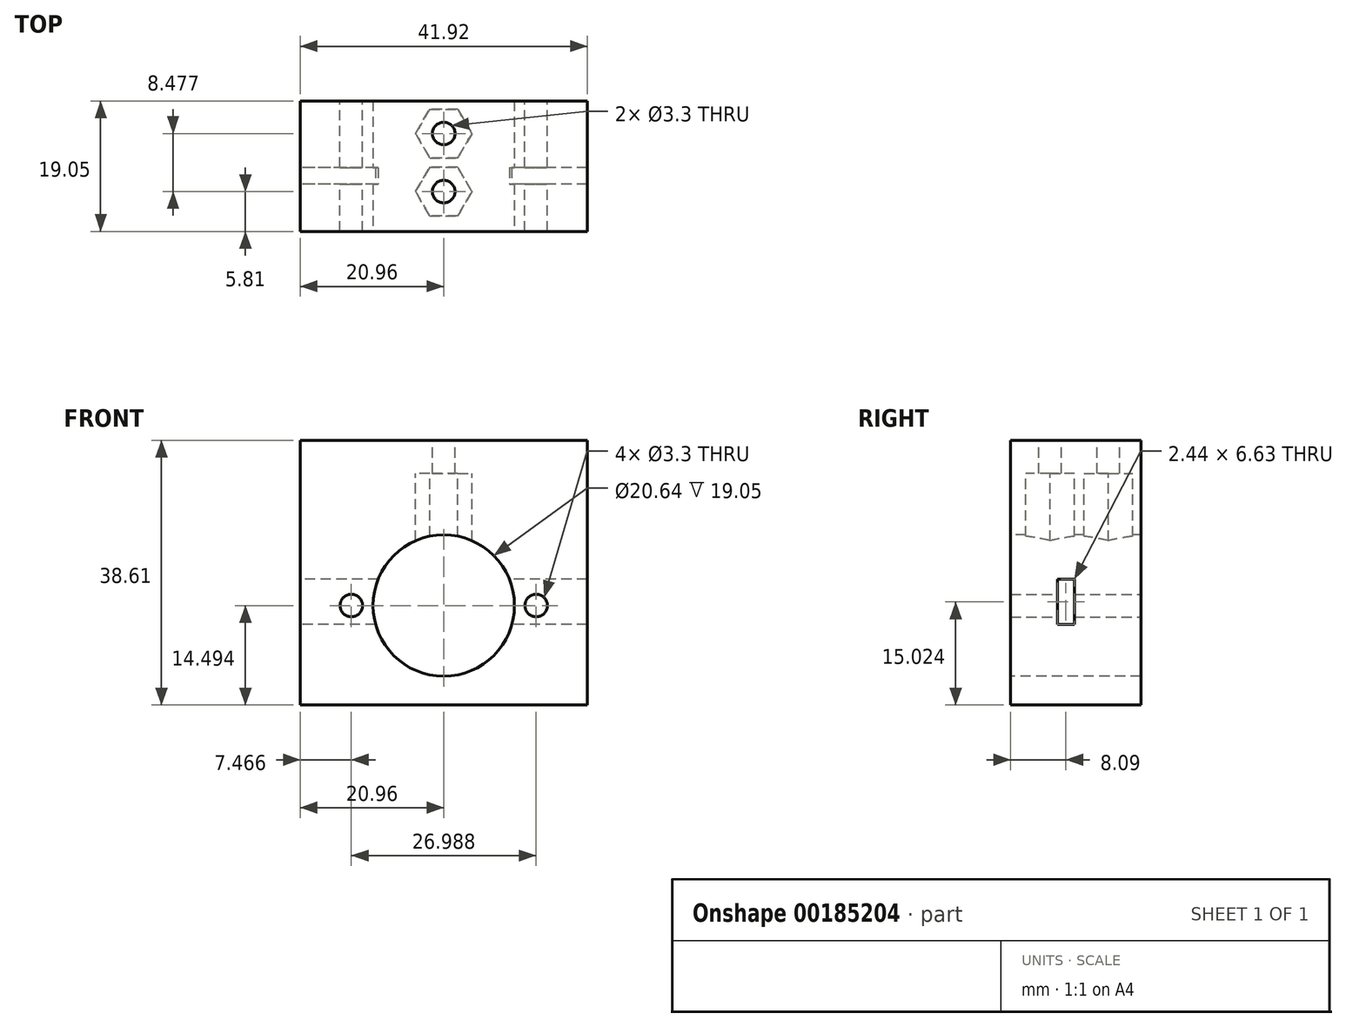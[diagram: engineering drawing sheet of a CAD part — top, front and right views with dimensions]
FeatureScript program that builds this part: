
annotation { "Feature Type Name" : "Feature", "Feature Type Description" : "" }
export const myFeature = defineFeature(function(context is Context, id is Id, definition is map)
    precondition{}
    {
        {
            var Q0;
            Q0=qCreatedBy(makeId("Front.planeOp"),FACE);
            var sketch = newSketch(context, id + "F0", { "sketchPlane" : qUnion([Q0])});
            skLineSegment(sketch, "E0.bottom", {"start": v(20.96, -17.65) * mm, "end": v(-20.96, -17.65) * mm});
            skLineSegment(sketch, "E0.top", {"start": v(20.96, 17.65) * mm, "end": v(-20.96, 17.65) * mm});
            skLineSegment(sketch, "E0.left", {"start": v(20.96, -17.65) * mm, "end": v(20.96, 17.65) * mm});
            skLineSegment(sketch, "E0.right", {"start": v(-20.96, -17.65) * mm, "end": v(-20.96, 17.65) * mm});
            skPoint(sketch, "E0.middle", {"position": v(0, 0) * mm});
            skSolve(sketch);
        }
        {
            var Q0;
            Q0=makeQuery(id+"F0.imprint","IMPRINT",FACE,{"disambiguationData":[TD([[makeQuery(id+"F0.imprint","IMPRINT",EDGE,{"derivedFrom":sQuery(id+"F0.wireOp",EDGE,"E0.bottom")}),-1.0]])]});
            extrude(context, id + "F1", {"entities" : qUnion([Q0]), "depth" : 19.05 * mm});
        }
        {
            var Q0;
            Q0=makeQuery(id+"F1.opExtrude","CAP_FACE",FACE,{"disambiguationData":[OSD([sQuery(id+"F0.wireOp",EDGE,"E0.bottom"),sQuery(id+"F0.wireOp",EDGE,"E0.top"),sQuery(id+"F0.wireOp",EDGE,"E0.left"),sQuery(id+"F0.wireOp",EDGE,"E0.right")])],"isStart":false});
            var sketch = newSketch(context, id + "F2", { "sketchPlane" : qUnion([Q0])});
            skCircle(sketch, "E1", {"center": v(0, -6.47) * mm, "radius": 10.32 * mm});
            skSolve(sketch);
        }
        {
            var Q0;
            Q0=makeQuery(id+"F2.imprint","IMPRINT",FACE,{"disambiguationData":[TD([[makeQuery(id+"F2.imprint","IMPRINT",EDGE,{"derivedFrom":sQuery(id+"F2.wireOp",EDGE,"E1")}),1.0]])]});
            var Q1;
            Q1=sQuery(id+"F2.wireOp",EDGE,"E1");
            var Q2;
            Q2=makeQuery(id+"F1.opExtrude","SWEPT_BODY",BODY,{"disambiguationData":[OSD([sQuery(id+"F0.wireOp",EDGE,"E0.bottom"),sQuery(id+"F0.wireOp",EDGE,"E0.top"),sQuery(id+"F0.wireOp",EDGE,"E0.left"),sQuery(id+"F0.wireOp",EDGE,"E0.right")])]});
            extrude(context, id + "F3", {"entities" : qUnion([Q0]), "operationType" : NewBodyOperationType.REMOVE, "surfaceEntities" : qUnion([Q1]), "endBound" : BoundingType.UP_TO_BODY, "oppositeDirection" : true, "endBoundEntityBody" : qUnion([Q2]), "depth" : 25.4 * mm});
        }
        {
            var Q0;
            Q0=makeQuery(id+"F1.opExtrude","SWEPT_FACE",FACE,{"disambiguationData":[OSD([sQuery(id+"F0.wireOp",EDGE,"E0.top")])]});
            var sketch = newSketch(context, id + "F4", { "sketchPlane" : qUnion([Q0])});
            skLineSegment(sketch, "E2", {"start": v(0, -4.76) * mm, "end": v(0, -14.29) * mm});
            skCircle(sketch, "E3.cCircle", {"center": v(0, -4.76) * mm, "radius": 3.56 * mm, "construction": true});
            skLineSegment(sketch, "E3.0", {"start": v(2.05, -8.32) * mm, "end": v(-2.05, -8.32) * mm});
            skLineSegment(sketch, "E3.1", {"start": v(-2.05, -8.32) * mm, "end": v(-4.1, -4.76) * mm});
            skLineSegment(sketch, "E3.2", {"start": v(-4.1, -4.76) * mm, "end": v(-2.05, -1.2) * mm});
            skLineSegment(sketch, "E3.3", {"start": v(-2.05, -1.2) * mm, "end": v(2.05, -1.2) * mm});
            skLineSegment(sketch, "E3.4", {"start": v(2.05, -1.2) * mm, "end": v(4.1, -4.76) * mm});
            skLineSegment(sketch, "E3.5", {"start": v(4.1, -4.76) * mm, "end": v(2.05, -8.32) * mm});
            skPoint(sketch, "E3.0.midPoint", {"position": v(0, -8.32) * mm});
            skCircle(sketch, "E4.cCircle", {"center": v(0, -13.24) * mm, "radius": 3.56 * mm, "construction": true});
            skPoint(sketch, "E4.0.midPoint", {"position": v(0.3, -16.78) * mm});
            skLineSegment(sketch, "E5.0", {"start": v(2.05, -16.8) * mm, "end": v(-2.05, -16.8) * mm});
            skLineSegment(sketch, "E5.1", {"start": v(-2.05, -16.8) * mm, "end": v(-4.1, -13.24) * mm});
            skLineSegment(sketch, "E5.2", {"start": v(-4.1, -13.24) * mm, "end": v(-2.05, -9.68) * mm});
            skLineSegment(sketch, "E5.3", {"start": v(-2.05, -9.68) * mm, "end": v(2.05, -9.68) * mm});
            skLineSegment(sketch, "E5.4", {"start": v(2.05, -9.68) * mm, "end": v(4.1, -13.24) * mm});
            skLineSegment(sketch, "E5.5", {"start": v(4.1, -13.24) * mm, "end": v(2.05, -16.8) * mm});
            skPoint(sketch, "E5.0.midPoint", {"position": v(0, -16.8) * mm});
            skSolve(sketch);
        }
        {
            var Q0;
            Q0=makeQuery(id+"F4.imprint","IMPRINT",FACE,{"disambiguationData":[TD([[makeQuery(id+"F4.imprint","IMPRINT",EDGE,{"derivedFrom":sQuery(id+"F4.wireOp",EDGE,"E5.0")}),-1.0]])]});
            var Q1;
            {var subQ1=sQuery(id+"F4.wireOp",EDGE,"E3.1");Q1=makeQuery(id+"F4.imprint","IMPRINT",FACE,{"disambiguationData":[TD([[makeQuery(id+"F4.imprint","IMPRINT",EDGE,{"derivedFrom":subQ1}),-1.0]])]});}
            extrude(context, id + "F5", {"entities" : qUnion([Q0, Q1]), "operationType" : NewBodyOperationType.REMOVE, "endBound" : BoundingType.UP_TO_NEXT, "oppositeDirection" : true, "depth" : 25.4 * mm});
        }
        {
            var Q0;
            Q0=makeQuery(id+"F1.opExtrude","SWEPT_FACE",FACE,{"disambiguationData":[OSD([sQuery(id+"F0.wireOp",EDGE,"E0.top")])]});
            extrude(context, id + "F6", {"entities" : qUnion([Q0]), "operationType" : NewBodyOperationType.ADD, "oppositeDirection" : true, "depth" : 5.84 * mm});
        }
        {
            var Q0;
            Q0=makeQuery(id+"F1.opExtrude","SWEPT_FACE",FACE,{"disambiguationData":[OSD([sQuery(id+"F0.wireOp",EDGE,"E0.left")])]});
            var sketch = newSketch(context, id + "F7", { "sketchPlane" : qUnion([Q0])});
            skLineSegment(sketch, "E6.0", {"start": v(-19.05, 12.83) * mm, "end": v(0, 12.83) * mm});
            skSolve(sketch);
        }
        {
            var Q0;
            {var subQ0=sQuery(id+"F7.wireOp",EDGE,"E6.0");Q0=makeQuery(id+"F7.imprint","IMPRINT",FACE,{"disambiguationData":[TD([[makeQuery(id+"F7.imprint","IMPRINT",EDGE,{"derivedFrom":subQ0}),1.0]])]});}
            extrude(context, id + "F8", {"entities" : qUnion([Q0]), "operationType" : NewBodyOperationType.ADD, "oppositeDirection" : true, "depth" : 25.4 * mm});
        }
        {
            var Q0;
            Q0=sQuery(id+"F4.wireOp",VERTEX,"E3.cCircle.center");
            var Q1;
            Q1=sQuery(id+"F4.wireOp",VERTEX,"E4.cCircle.center");
            var Q2;
            Q2=makeQuery(id+"F1.opExtrude","SWEPT_BODY",BODY,{"disambiguationData":[OSD([sQuery(id+"F0.wireOp",EDGE,"E0.bottom"),sQuery(id+"F0.wireOp",EDGE,"E0.top"),sQuery(id+"F0.wireOp",EDGE,"E0.left"),sQuery(id+"F0.wireOp",EDGE,"E0.right")])]});
            hole(context, id + "F9", {"style" : HoleStyle.SIMPLE, "endStyle" : HoleEndStyle.BLIND, "standardTappedOrClearance" : lookupTablePath({ "standard" : "ISO", "fit" : "Normal", "size" : "M3", "type" : "Clearance" }), "standardBlindInLast" : lookupTablePath({ "fit" : "Standard", "standard" : "ISO", "size" : "M3", "type" : "Clearance" }), "holeDiameter" : 3.3 * mm, "holeDepth" : 12.7 * mm, "startFromSketch" : true, "locations" : qUnion([Q0, Q1]), "scope" : qUnion([Q2])});
        }
        {
            var Q0;
            Q0=makeQuery(id+"F1.opExtrude","CAP_FACE",FACE,{"disambiguationData":[OSD([sQuery(id+"F0.wireOp",EDGE,"E0.bottom"),sQuery(id+"F0.wireOp",EDGE,"E0.top"),sQuery(id+"F0.wireOp",EDGE,"E0.left"),sQuery(id+"F0.wireOp",EDGE,"E0.right")])],"isStart":true});
            var sketch = newSketch(context, id + "F10", { "sketchPlane" : qUnion([Q0])});
            skLineSegment(sketch, "E7", {"start": v(-13.5, -6.47) * mm, "end": v(13.5, -6.47) * mm});
            skSolve(sketch);
        }
        {
            var Q0;
            Q0=sQuery(id+"F10.wireOp",VERTEX,"E7.start");
            var Q1;
            Q1=sQuery(id+"F10.wireOp",VERTEX,"E7.end");
            var Q2;
            Q2=makeQuery(id+"F1.opExtrude","SWEPT_BODY",BODY,{"disambiguationData":[OSD([sQuery(id+"F0.wireOp",EDGE,"E0.bottom"),sQuery(id+"F0.wireOp",EDGE,"E0.top"),sQuery(id+"F0.wireOp",EDGE,"E0.left"),sQuery(id+"F0.wireOp",EDGE,"E0.right")])]});
            hole(context, id + "F11", {"style" : HoleStyle.SIMPLE, "endStyle" : HoleEndStyle.THROUGH, "holeDiameter" : 3.3 * mm, "startFromSketch" : true, "locations" : qUnion([Q0, Q1]), "scope" : qUnion([Q2]), "isTappedThrough" : true});
        }
        {
            var Q0;
            Q0=makeQuery(id+"F1.opExtrude","SWEPT_FACE",FACE,{"disambiguationData":[OSD([sQuery(id+"F0.wireOp",EDGE,"E0.right")])]});
            var sketch = newSketch(context, id + "F12", { "sketchPlane" : qUnion([Q0])});
            skLineSegment(sketch, "E8.bottom", {"start": v(12.18, -2.62) * mm, "end": v(9.74, -2.62) * mm});
            skLineSegment(sketch, "E8.top", {"start": v(12.18, -9.25) * mm, "end": v(9.74, -9.25) * mm});
            skLineSegment(sketch, "E8.left", {"start": v(12.18, -2.62) * mm, "end": v(12.18, -9.25) * mm});
            skLineSegment(sketch, "E8.right", {"start": v(9.74, -2.62) * mm, "end": v(9.74, -9.25) * mm});
            skPoint(sketch, "E8.middle", {"position": v(10.96, -5.94) * mm});
            skSolve(sketch);
        }
        {
            var Q0;
            Q0=makeQuery(id+"F12.imprint","IMPRINT",FACE,{"disambiguationData":[TD([[makeQuery(id+"F12.imprint","IMPRINT",EDGE,{"derivedFrom":sQuery(id+"F12.wireOp",EDGE,"E8.bottom")}),1.0]])]});
            extrude(context, id + "F13", {"entities" : qUnion([Q0]), "operationType" : NewBodyOperationType.REMOVE, "oppositeDirection" : true, "depth" : 59.92 * mm});
        }
        {
            var Q0;
            Q0=makeQuery(id+"F1.opExtrude","SWEPT_FACE",FACE,{"disambiguationData":[OSD([sQuery(id+"F0.wireOp",EDGE,"E0.bottom")])]});
            extrude(context, id + "F14", {"entities" : qUnion([Q0]), "operationType" : NewBodyOperationType.ADD, "depth" : 3.3 * mm});
        }
    });
